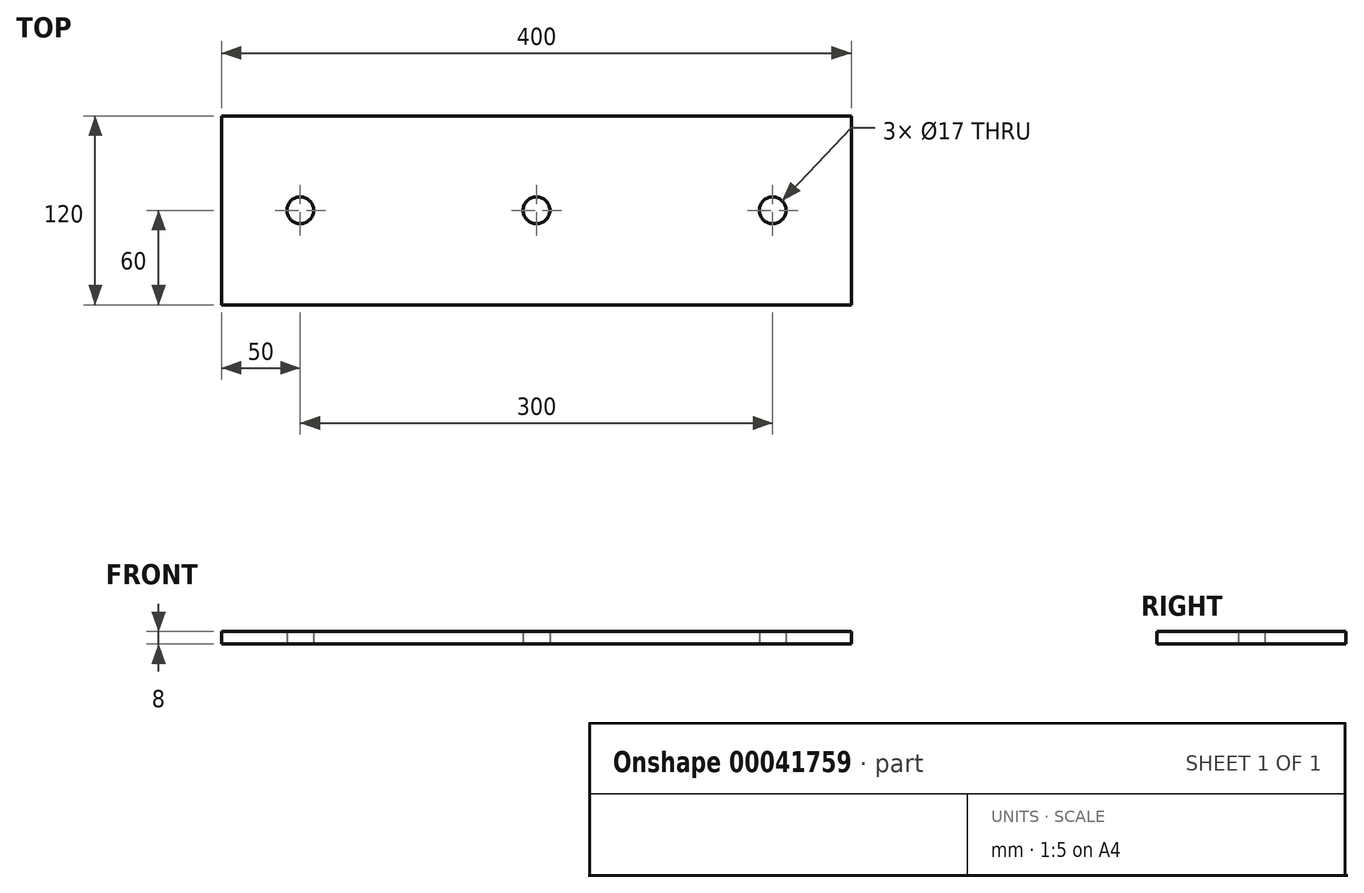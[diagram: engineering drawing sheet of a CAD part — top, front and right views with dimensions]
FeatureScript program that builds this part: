
annotation { "Feature Type Name" : "Feature", "Feature Type Description" : "" }
export const myFeature = defineFeature(function(context is Context, id is Id, definition is map)
    precondition{}
    {
        {
            var Q0;
            Q0=qCreatedBy(makeId("Top.planeOp"),FACE);
            var sketch = newSketch(context, id + "F0", { "sketchPlane" : qUnion([Q0])});
            skLineSegment(sketch, "E0.rect.bottom", {"start": v(200, 60) * mm, "end": v(-200, 60) * mm});
            skLineSegment(sketch, "E0.rect.top", {"start": v(200, -60) * mm, "end": v(-200, -60) * mm});
            skLineSegment(sketch, "E0.rect.left", {"start": v(200, 60) * mm, "end": v(200, -60) * mm});
            skLineSegment(sketch, "E0.rect.right", {"start": v(-200, 60) * mm, "end": v(-200, -60) * mm});
            skPoint(sketch, "E0.rect.middle", {"position": v(0, 0) * mm});
            skCircle(sketch, "E1", {"center": v(0, 0) * mm, "radius": 8.5 * mm});
            skCircle(sketch, "E2", {"center": v(-150, 0) * mm, "radius": 8.5 * mm});
            skCircle(sketch, "E3", {"center": v(150, 0) * mm, "radius": 8.5 * mm});
            skSolve(sketch);
        }
        {
            var Q0;
            Q0=makeQuery(id+"F0.imprint","IMPRINT",FACE,{"disambiguationData":[TD([[makeQuery(id+"F0.imprint","IMPRINT",EDGE,{"derivedFrom":sQuery(id+"F0.wireOp",EDGE,"E0.rect.bottom")}),1.0]])]});
            extrude(context, id + "F1", {"entities" : qUnion([Q0]), "depth" : 8 * mm});
        }
    });
